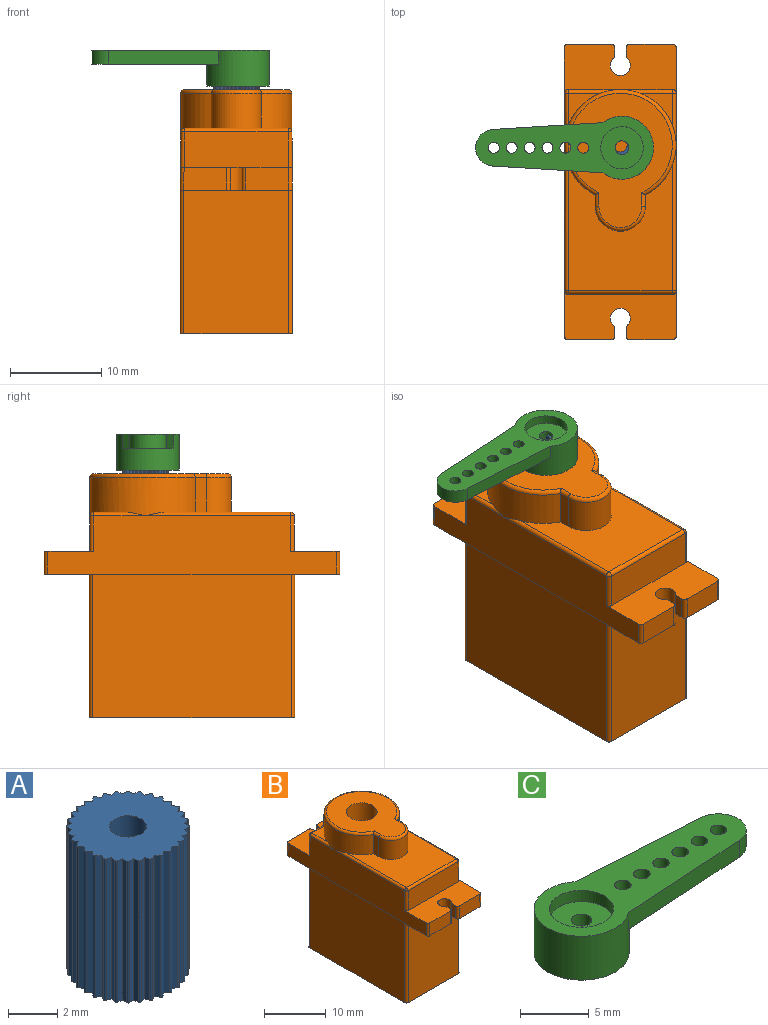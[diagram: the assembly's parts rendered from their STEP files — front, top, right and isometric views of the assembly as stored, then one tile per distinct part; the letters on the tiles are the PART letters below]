
ASSEMBLY  parts=3 mates=1
PART A: 99 faces, bbox 5x5x7.1 mm
  f0: plane 5x5mm, normal (0,0,-1), area 16.5mm2, adj f1,f2,f3,f4,f5,f6,f7,f8
  f1: plane 7.05x0.2mm, normal (-0.8,0.6,0), area 1.7mm2, adj f0,f2,f94,f95
  f2: cylinder r=0.08mm len=7.05mm, axis (0,0,-1), area 0.9mm2, adj f0,f1,f3,f94
  f3: plane 7.05x0.21mm, normal (-0.51,-0.86,0), area 1.7mm2, adj f0,f2,f4,f94
  f4: plane 7.05x0.22mm, normal (-0.9,0.43,0), area 1.7mm2, adj f0,f3,f5,f94
  f5: cylinder r=0.08mm len=7.05mm, axis (0,0,-1), area 0.9mm2, adj f0,f4,f6,f94
  f6: plane 7.05x0.23mm, normal (-0.33,-0.94,0), area 1.7mm2, adj f0,f5,f7,f94
  f7: plane 7.05x0.24mm, normal (-0.97,0.25,0), area 1.7mm2, adj f0,f6,f8,f94
  f8: cylinder r=0.08mm len=7.05mm, axis (0,0,-1), area 0.9mm2, adj f0,f7,f9,f94
  f9: plane 7.05x0.25mm, normal (-0.14,-0.99,0), area 1.7mm2, adj f0,f8,f10,f94
  f10: plane 7.05x0.25mm, normal (-1,0.05,0), area 1.7mm2, adj f0,f9,f11,f94
  f11: cylinder r=0.08mm len=7.05mm, axis (0,0,-1), area 0.9mm2, adj f0,f10,f12,f94
  f12: plane 7.05x0.25mm, normal (0.05,-1,0), area 1.7mm2, adj f0,f11,f13,f94
  f13: plane 7.05x0.25mm, normal (-0.99,-0.14,0), area 1.7mm2, adj f0,f12,f14,f94
  f14: cylinder r=0.08mm len=7.05mm, axis (0,0,-1), area 0.9mm2, adj f0,f13,f15,f94
  f15: plane 7.05x0.24mm, normal (0.25,-0.97,0), area 1.7mm2, adj f0,f14,f16,f94
  f16: plane 7.05x0.23mm, normal (-0.94,-0.33,0), area 1.7mm2, adj f0,f15,f17,f94
  f17: cylinder r=0.08mm len=7.05mm, axis (0,0,-1), area 0.9mm2, adj f0,f16,f18,f94
  f18: plane 7.05x0.22mm, normal (0.43,-0.9,0), area 1.7mm2, adj f0,f17,f19,f94
  f19: plane 7.05x0.21mm, normal (-0.86,-0.51,0), area 1.7mm2, adj f0,f18,f20,f94
  f20: cylinder r=0.08mm len=7.05mm, axis (0,0,-1), area 0.9mm2, adj f0,f19,f21,f94
  f21: plane 7.05x0.2mm, normal (0.6,-0.8,0), area 1.7mm2, adj f0,f20,f22,f94
  f22: plane 7.05x0.18mm, normal (-0.74,-0.67,0), area 1.7mm2, adj f0,f21,f23,f94
  f23: cylinder r=0.08mm len=7.05mm, axis (0,0,-1), area 0.9mm2, adj f0,f22,f24,f94
  f24: plane 7.05x0.18mm, normal (0.74,-0.67,0), area 1.7mm2, adj f0,f23,f25,f94
  f25: plane 7.05x0.2mm, normal (-0.6,-0.8,0), area 1.7mm2, adj f0,f24,f26,f94
  f26: cylinder r=0.08mm len=7.05mm, axis (0,0,-1), area 0.9mm2, adj f0,f25,f27,f94
  f27: plane 7.05x0.21mm, normal (0.86,-0.51,0), area 1.7mm2, adj f0,f26,f28,f94
  f28: plane 7.05x0.22mm, normal (-0.43,-0.9,0), area 1.7mm2, adj f0,f27,f29,f94
  f29: cylinder r=0.08mm len=7.05mm, axis (0,0,-1), area 0.9mm2, adj f0,f28,f30,f94
  f30: plane 7.05x0.23mm, normal (0.94,-0.33,0), area 1.7mm2, adj f0,f29,f31,f94
  f31: plane 7.05x0.24mm, normal (-0.25,-0.97,0), area 1.7mm2, adj f0,f30,f32,f94
  f32: cylinder r=0.08mm len=7.05mm, axis (0,0,-1), area 0.9mm2, adj f0,f31,f33,f94
  f33: plane 7.05x0.25mm, normal (0.99,-0.14,0), area 1.7mm2, adj f0,f32,f34,f94
  f34: plane 7.05x0.25mm, normal (-0.05,-1,0), area 1.7mm2, adj f0,f33,f35,f94
  f35: cylinder r=0.08mm len=7.05mm, axis (0,0,-1), area 0.9mm2, adj f0,f34,f36,f94
  f36: plane 7.05x0.25mm, normal (1,0.05,0), area 1.7mm2, adj f0,f35,f37,f94
  f37: plane 7.05x0.25mm, normal (0.14,-0.99,0), area 1.7mm2, adj f0,f36,f38,f94
  f38: cylinder r=0.08mm len=7.05mm, axis (0,0,-1), area 0.9mm2, adj f0,f37,f39,f94
  f39: plane 7.05x0.24mm, normal (0.97,0.25,0), area 1.7mm2, adj f0,f38,f40,f94
  f40: plane 7.05x0.23mm, normal (0.33,-0.94,0), area 1.7mm2, adj f0,f39,f41,f94
  f41: cylinder r=0.08mm len=7.05mm, axis (0,0,-1), area 0.9mm2, adj f0,f40,f42,f94
  f42: plane 7.05x0.22mm, normal (0.9,0.43,0), area 1.7mm2, adj f0,f41,f43,f94
  f43: plane 7.05x0.21mm, normal (0.51,-0.86,0), area 1.7mm2, adj f0,f42,f44,f94
  f44: cylinder r=0.08mm len=7.05mm, axis (0,0,-1), area 0.9mm2, adj f0,f43,f45,f94
  f45: plane 7.05x0.2mm, normal (0.8,0.6,0), area 1.7mm2, adj f0,f44,f46,f94
  f46: plane 7.05x0.18mm, normal (0.67,-0.74,0), area 1.7mm2, adj f0,f45,f47,f94
  f47: cylinder r=0.08mm len=7.05mm, axis (0,0,-1), area 0.9mm2, adj f0,f46,f48,f94
  f48: plane 7.05x0.18mm, normal (0.67,0.74,0), area 1.7mm2, adj f0,f47,f49,f94
  f49: plane 7.05x0.2mm, normal (0.8,-0.6,0), area 1.7mm2, adj f0,f48,f50,f94
  f50: cylinder r=0.08mm len=7.05mm, axis (0,0,-1), area 0.9mm2, adj f0,f49,f51,f94
  f51: plane 7.05x0.21mm, normal (0.51,0.86,0), area 1.7mm2, adj f0,f50,f52,f94
  f52: plane 7.05x0.22mm, normal (0.9,-0.43,0), area 1.7mm2, adj f0,f51,f53,f94
  f53: cylinder r=0.08mm len=7.05mm, axis (0,0,-1), area 0.9mm2, adj f0,f52,f54,f94
  f54: plane 7.05x0.23mm, normal (0.33,0.94,0), area 1.7mm2, adj f0,f53,f55,f94
  f55: plane 7.05x0.24mm, normal (0.97,-0.25,0), area 1.7mm2, adj f0,f54,f56,f94
  f56: cylinder r=0.08mm len=7.05mm, axis (0,0,-1), area 0.9mm2, adj f0,f55,f57,f94
  f57: plane 7.05x0.25mm, normal (0.14,0.99,0), area 1.7mm2, adj f0,f56,f58,f94
  f58: plane 7.05x0.25mm, normal (1,-0.05,0), area 1.7mm2, adj f0,f57,f59,f94
  f59: cylinder r=0.08mm len=7.05mm, axis (0,0,-1), area 0.9mm2, adj f0,f58,f60,f94
  f60: plane 7.05x0.25mm, normal (-0.05,1,0), area 1.7mm2, adj f0,f59,f61,f94
  f61: plane 7.05x0.25mm, normal (0.99,0.14,0), area 1.7mm2, adj f0,f60,f62,f94
  f62: cylinder r=0.08mm len=7.05mm, axis (0,0,-1), area 0.9mm2, adj f0,f61,f63,f94
  f63: plane 7.05x0.24mm, normal (-0.25,0.97,0), area 1.7mm2, adj f0,f62,f64,f94
  f64: plane 7.05x0.23mm, normal (0.94,0.33,0), area 1.7mm2, adj f0,f63,f65,f94
  f65: cylinder r=0.08mm len=7.05mm, axis (0,0,-1), area 0.9mm2, adj f0,f64,f66,f94
  f66: plane 7.05x0.22mm, normal (-0.43,0.9,0), area 1.7mm2, adj f0,f65,f67,f94
  f67: plane 7.05x0.21mm, normal (0.86,0.51,0), area 1.7mm2, adj f0,f66,f68,f94
  f68: cylinder r=0.08mm len=7.05mm, axis (0,0,-1), area 0.9mm2, adj f0,f67,f69,f94
  f69: plane 7.05x0.2mm, normal (-0.6,0.8,0), area 1.7mm2, adj f0,f68,f70,f94
  f70: plane 7.05x0.18mm, normal (0.74,0.67,0), area 1.7mm2, adj f0,f69,f71,f94
  f71: cylinder r=0.08mm len=7.05mm, axis (0,0,-1), area 0.9mm2, adj f0,f70,f72,f94
  f72: plane 7.05x0.18mm, normal (-0.74,0.67,0), area 1.7mm2, adj f0,f71,f73,f94
  f73: plane 7.05x0.2mm, normal (0.6,0.8,0), area 1.7mm2, adj f0,f72,f74,f94
  f74: cylinder r=0.08mm len=7.05mm, axis (0,0,-1), area 0.9mm2, adj f0,f73,f75,f94
  f75: plane 7.05x0.21mm, normal (-0.86,0.51,0), area 1.7mm2, adj f0,f74,f76,f94
  f76: plane 7.05x0.22mm, normal (0.43,0.9,0), area 1.7mm2, adj f0,f75,f77,f94
  f77: cylinder r=0.08mm len=7.05mm, axis (0,0,-1), area 0.9mm2, adj f0,f76,f78,f94
  f78: plane 7.05x0.23mm, normal (-0.94,0.33,0), area 1.7mm2, adj f0,f77,f79,f94
  f79: plane 7.05x0.24mm, normal (0.25,0.97,0), area 1.7mm2, adj f0,f78,f80,f94
  f80: cylinder r=0.08mm len=7.05mm, axis (0,0,-1), area 0.9mm2, adj f0,f79,f81,f94
  f81: plane 7.05x0.25mm, normal (-0.99,0.14,0), area 1.7mm2, adj f0,f80,f82,f94
  f82: plane 7.05x0.25mm, normal (0.05,1,0), area 1.7mm2, adj f0,f81,f83,f94
  f83: cylinder r=0.08mm len=7.05mm, axis (0,0,-1), area 0.9mm2, adj f0,f82,f84,f94
  f84: plane 7.05x0.25mm, normal (-1,-0.05,0), area 1.7mm2, adj f0,f83,f85,f94
  f85: plane 7.05x0.25mm, normal (-0.14,0.99,0), area 1.7mm2, adj f0,f84,f86,f94
  f86: cylinder r=0.08mm len=7.05mm, axis (0,0,-1), area 0.9mm2, adj f0,f85,f87,f94
  f87: plane 7.05x0.24mm, normal (-0.97,-0.25,0), area 1.7mm2, adj f0,f86,f88,f94
  f88: plane 7.05x0.23mm, normal (-0.33,0.94,0), area 1.7mm2, adj f0,f87,f89,f94
  f89: cylinder r=0.08mm len=7.05mm, axis (0,0,-1), area 0.9mm2, adj f0,f88,f90,f94
  f90: plane 7.05x0.22mm, normal (-0.9,-0.43,0), area 1.7mm2, adj f0,f89,f91,f94
  f91: plane 7.05x0.21mm, normal (-0.51,0.86,0), area 1.7mm2, adj f0,f90,f92,f94
  f92: cylinder r=0.08mm len=7.05mm, axis (0,0,-1), area 0.9mm2, adj f0,f91,f93,f94
  f93: plane 7.05x0.2mm, normal (-0.8,-0.6,0), area 1.7mm2, adj f0,f92,f94,f96
  f94: plane 5x5mm, normal (0,0,1), area 16.5mm2, adj f1,f2,f3,f4,f5,f6,f7,f8
  f95: plane 7.05x0.18mm, normal (-0.67,-0.74,0), area 1.7mm2, adj f0,f1,f94,f97
  f96: plane 7.05x0.18mm, normal (-0.67,0.74,0), area 1.7mm2, adj f0,f93,f94,f97
  f97: cylinder r=0.08mm len=7.05mm, axis (0,0,-1), area 0.9mm2, adj f0,f94,f95,f96
  f98: cylinder r=0.75mm len=7.05mm, axis (0,0,-1), area 33.2mm2, adj f0,f94
PART B: 64 faces, bbox 13.2x32.4x26.7 mm
  f0: plane 3.52x3.52mm, normal (0,0,1), area 4.4mm2, adj f4,f7,f57
  f1: plane 3.52x3.52mm, normal (0,0,1), area 4.4mm2, adj f5,f8,f57
  f2: plane 13.72x11.39mm, normal (0,0,1), area 107.7mm2, adj f3,f6,f47,f53,f54,f57,f58
  f3: cylinder r=0.4mm len=15.89mm, axis (0,1,0), area 9.3mm2, adj f2,f17,f45,f57
  f4: cylinder r=0.4mm len=5.69mm, axis (0,1,0), area 2.9mm2, adj f0,f17,f50,f57
  f5: cylinder r=0.4mm len=5.69mm, axis (0,1,0), area 2.9mm2, adj f1,f15,f51,f57
  f6: cylinder r=0.4mm len=15.89mm, axis (0,1,0), area 9.3mm2, adj f2,f15,f49,f57
  f7: cylinder r=0.4mm len=5.69mm, axis (-1,0,0), area 2.9mm2, adj f0,f16,f50,f57
  f8: cylinder r=0.4mm len=5.69mm, axis (-1,0,0), area 2.9mm2, adj f1,f16,f51,f57
  f9: plane 4.73x2.5mm, normal (0,1,0.01), area 11.8mm2, adj f11,f12,f32,f36
  f10: plane 4.73x2.5mm, normal (0,1,0.01), area 11.8mm2, adj f11,f12,f33,f37
  f11: plane 12.3x5.35mm, normal (0,0,-1), area 55.4mm2, adj f9,f10,f15,f17,f22,f29,f30,f31
  f12: plane 12.26x5.35mm, normal (0,0,1), area 55.2mm2, adj f9,f10,f15,f16,f17,f29,f30,f31
  f13: plane 4.73x2.5mm, normal (0,-1,0.01), area 11.8mm2, adj f14,f25,f34,f38
  f14: plane 12.26x5.35mm, normal (0,0,1), area 55.2mm2, adj f13,f15,f17,f18,f24,f26,f27,f28
  f15: plane 31.6x6.4mm, normal (1,0,0.01), area 163.4mm2, adj f5,f6,f11,f12,f14,f23,f25,f36
  f16: plane 11.46x3.9mm, normal (0,1,0.01), area 44.6mm2, adj f7,f8,f12,f48,f52
  f17: plane 31.6x6.4mm, normal (-1,0,0.01), area 163.4mm2, adj f3,f4,f11,f12,f14,f21,f25,f37
  f18: plane 11.46x3.9mm, normal (0,-1,0.01), area 44.6mm2, adj f14,f44,f46,f47
  f19: plane 22.5x12.3mm, normal (0,0,-1), area 276.6mm2, adj f20,f21,f22,f23,f40,f41,f42,f43
  f20: plane 15.7x11.5mm, normal (0,-1,0), area 180.5mm2, adj f19,f25,f42,f43
  f21: plane 21.7x15.7mm, normal (-1,0,0), area 340.7mm2, adj f17,f19,f41,f42
  f22: plane 15.7x11.5mm, normal (0,1,0), area 180.5mm2, adj f11,f19,f40,f41
  f23: plane 21.7x15.7mm, normal (1,0,0), area 340.7mm2, adj f15,f19,f40,f43
  f24: plane 4.73x2.5mm, normal (0,-1,0.01), area 11.8mm2, adj f14,f25,f35,f39
  f25: plane 12.3x5.35mm, normal (0,0,-1), area 55.4mm2, adj f13,f15,f17,f20,f24,f26,f27,f28
  f26: cylinder r=1.1mm len=2.5mm, axis (0,0,1), area 14mm2, adj f14,f25,f27,f28
  f27: plane 2.5x1.04mm, normal (1,0,0), area 2.6mm2, adj f14,f25,f26,f34
  f28: plane 2.5x1.04mm, normal (-1,0,0), area 2.6mm2, adj f14,f25,f26,f35
  f29: plane 2.5x1.04mm, normal (-1,0,0), area 2.6mm2, adj f11,f12,f31,f32
  f30: plane 2.5x1.04mm, normal (1,0,0), area 2.6mm2, adj f11,f12,f31,f33
  f31: cylinder r=1.1mm len=2.5mm, axis (0,0,1), area 14mm2, adj f11,f12,f29,f30
  f32: cylinder r=0.4mm len=2.51mm, axis (0,0.01,-1), area 1.6mm2, adj f9,f11,f12,f29
  f33: cylinder r=0.4mm len=2.51mm, axis (0,-0.01,1), area 1.6mm2, adj f10,f11,f12,f30
  f34: cylinder r=0.4mm len=2.51mm, axis (0,0.01,1), area 1.6mm2, adj f13,f14,f25,f27
  f35: cylinder r=0.4mm len=2.51mm, axis (0,-0.01,-1), area 1.6mm2, adj f14,f24,f25,f28
  f36: cylinder r=0.4mm len=2.5mm, axis (0.01,0.01,-1), area 1.6mm2, adj f9,f11,f12,f15
  f37: cylinder r=0.4mm len=2.5mm, axis (-0.01,0.01,-1), area 1.6mm2, adj f10,f11,f12,f17
  f38: cylinder r=0.4mm len=2.5mm, axis (-0.01,-0.01,-1), area 1.6mm2, adj f13,f14,f17,f25
  f39: cylinder r=0.4mm len=2.5mm, axis (0.01,-0.01,-1), area 1.6mm2, adj f14,f15,f24,f25
  f40: cylinder r=0.4mm len=15.7mm, axis (0,0,-1), area 9.9mm2, adj f11,f19,f22,f23
  f41: cylinder r=0.4mm len=15.7mm, axis (0,0,1), area 9.9mm2, adj f11,f19,f21,f22
  f42: cylinder r=0.4mm len=15.7mm, axis (0,0,-1), area 9.9mm2, adj f19,f20,f21,f25
  f43: cylinder r=0.4mm len=15.7mm, axis (0,0,1), area 9.9mm2, adj f19,f20,f23,f25
  f44: cylinder r=0.4mm len=3.91mm, axis (-0.01,-0.01,-1), area 2.5mm2, adj f14,f17,f18,f45
  f45: sphere r=0.4mm, area 0.2mm2, adj f3,f44,f47
  f46: cylinder r=0.4mm len=3.91mm, axis (0.01,-0.01,-1), area 2.5mm2, adj f14,f15,f18,f49
  f47: cylinder r=0.4mm len=11.39mm, axis (-1,0,0), area 7.1mm2, adj f2,f18,f45,f49
  f48: cylinder r=0.4mm len=3.91mm, axis (-0.01,0.01,-1), area 2.5mm2, adj f12,f16,f17,f50
  f49: sphere r=0.4mm, area 0.2mm2, adj f6,f46,f47
  f50: sphere r=0.4mm, area 0.2mm2, adj f4,f7,f48
  f51: sphere r=0.4mm, area 0.2mm2, adj f5,f8,f52
  f52: cylinder r=0.4mm len=3.91mm, axis (0.01,0.01,-1), area 2.5mm2, adj f12,f15,f16,f51
  f53: plane 3.8x1.22mm, normal (-1,0,0), area 4.6mm2, adj f2,f54,f57,f61
  f54: cylinder r=2.75mm len=5.5mm, axis (0,0,-1), area 32.8mm2, adj f2,f53,f58,f63
  f55: plane 14.7x11.39mm, normal (0,0,1), area 96.2mm2, adj f56,f60,f61,f62,f63
  f56: cylinder r=2.5mm len=5mm, axis (0,0,-1), area 66mm2, adj f55,f59
  f57: cylinder r=6.09mm len=12.19mm, axis (0,0,-1), area 125.9mm2, adj f0,f1,f2,f3,f4,f5,f6,f7
  f58: plane 3.8x1.22mm, normal (1,0,0), area 4.6mm2, adj f2,f54,f57,f62
  f59: plane 5x5mm, normal (0,0,1), area 19.6mm2, adj f56
  f60: torus R=5.69mm, axis (0,0,1), area 20.1mm2, adj f55,f57,f61,f62
  f61: cylinder r=0.4mm len=1.47mm, axis (0,1,0), area 0.8mm2, adj f53,f55,f60,f63
  f62: cylinder r=0.4mm len=1.47mm, axis (0,-1,0), area 0.8mm2, adj f55,f58,f60,f63
  f63: torus R=2.35mm, axis (0,0,1), area 5.1mm2, adj f54,f55,f61,f62
PART C: 18 faces, bbox 19.5x6.9x3.9 mm
  f0: plane 4.65x4.65mm, normal (0,0,1), area 15.2mm2, adj f1,f7
  f1: cylinder r=0.75mm len=1.5mm, axis (0,0,-1), area 4.9mm2, adj f0,f2
  f2: plane 5x5mm, normal (0,0,-1), area 17.9mm2, adj f1,f3
  f3: cylinder r=2.5mm len=5mm, axis (0,0,-1), area 29.1mm2, adj f2,f4
  f4: plane 6.9x6.9mm, normal (0,0,-1), area 17.8mm2, adj f3,f5
  f5: cylinder r=3.45mm len=6.9mm, axis (0,0,-1), area 75mm2, adj f4,f6,f8,f9,f11
  f6: plane 19.5x6.9mm, normal (0,0,1), area 71.6mm2, adj f5,f7,f8,f9,f10,f12,f13,f14
  f7: cylinder r=2.32mm len=4.65mm, axis (0,0,-1), area 14.6mm2, adj f0,f6
  f8: plane 12.09x1.5mm, normal (0.06,1,0), area 18.2mm2, adj f5,f6,f10,f11
  f9: plane 12.09x1.5mm, normal (0.06,-1,0), area 18.2mm2, adj f5,f6,f10,f11
  f10: cylinder r=2mm len=4mm, axis (0,0,1), area 9.1mm2, adj f6,f8,f9,f11
  f11: plane 13.97x5.5mm, normal (0,0,-1), area 51.2mm2, adj f5,f8,f9,f10,f12,f13,f14,f15
  f12: cylinder r=0.6mm len=1.5mm, axis (0,0,1), area 5.7mm2, adj f6,f11
  f13: cylinder r=0.6mm len=1.5mm, axis (0,0,1), area 5.7mm2, adj f6,f11
  f14: cylinder r=0.6mm len=1.5mm, axis (0,0,1), area 5.7mm2, adj f6,f11
  f15: cylinder r=0.6mm len=1.5mm, axis (0,0,1), area 5.7mm2, adj f6,f11
  f16: cylinder r=0.6mm len=1.5mm, axis (0,0,1), area 5.7mm2, adj f6,f11
  f17: cylinder r=0.6mm len=1.5mm, axis (0,0,1), area 5.7mm2, adj f6,f11
PLACE A at identity
PLACE B at identity fixed
PLACE C rot(axis=(0,0,-1),180deg) t=(0.18,9.92,-0.57)mm
MATE revolute B.f56 <-> A.f98  axis (0,0,-1) through (0,5.1,6.8)mm
